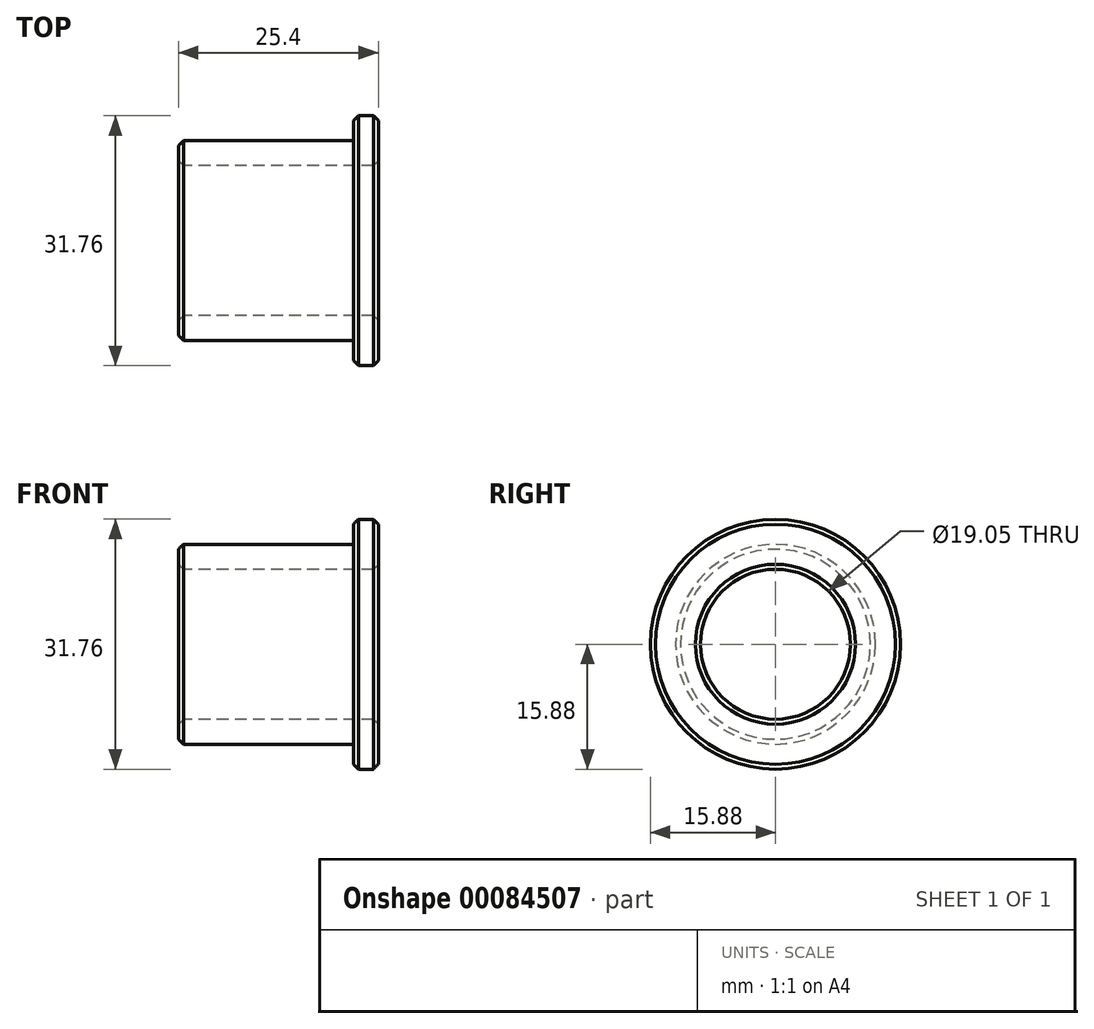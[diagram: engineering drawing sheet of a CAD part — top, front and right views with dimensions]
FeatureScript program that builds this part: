
annotation { "Feature Type Name" : "Feature", "Feature Type Description" : "" }
export const myFeature = defineFeature(function(context is Context, id is Id, definition is map)
    precondition{}
    {
        {
            var Q0;
            Q0=qCreatedBy(makeId("Front.planeOp"),FACE);
            var sketch = newSketch(context, id + "F0", { "sketchPlane" : qUnion([Q0])});
            skLineSegment(sketch, "E0", {"start": v(0, 9.52) * mm, "end": v(0, 12.7) * mm});
            skLineSegment(sketch, "E1", {"start": v(0, 12.7) * mm, "end": v(22.23, 12.7) * mm});
            skLineSegment(sketch, "E2", {"start": v(22.23, 12.7) * mm, "end": v(22.23, 15.88) * mm});
            skLineSegment(sketch, "E3", {"start": v(22.23, 15.88) * mm, "end": v(25.4, 15.88) * mm});
            skLineSegment(sketch, "E4", {"start": v(25.4, 15.88) * mm, "end": v(25.4, 9.53) * mm});
            skLineSegment(sketch, "E5", {"start": v(25.4, 9.53) * mm, "end": v(0, 9.52) * mm});
            skLineSegment(sketch, "E6", {"start": v(0, 0) * mm, "end": v(20.73, 0) * mm, "construction": true});
            skSolve(sketch);
        }
        {
            var Q0;
            Q0 = qSketchRegion(id + "F0", true);
            var Q1;
            Q1=sQuery(id+"F0.wireOp",EDGE,"E6");
            revolve(context, id + "F1", {"entities" : qUnion([Q0]), "axis" : qUnion([Q1]), "revolveType" : RevolveType.FULL});
        }
        {
            var Q0;
            Q0=makeQuery(id+"F1.opRevolve","SWEPT_EDGE",EDGE,{"disambiguationData":[OSD([sQuery(id+"F0.wireOp",EDGE,"E3"),sQuery(id+"F0.wireOp",EDGE,"E4")])]});
            var Q1;
            Q1=makeQuery(id+"F1.opRevolve","SWEPT_EDGE",EDGE,{"disambiguationData":[OSD([sQuery(id+"F0.wireOp",EDGE,"E0"),sQuery(id+"F0.wireOp",EDGE,"E1")])]});
            var Q2;
            Q2=makeQuery(id+"F1.opRevolve","SWEPT_EDGE",EDGE,{"disambiguationData":[OSD([sQuery(id+"F0.wireOp",EDGE,"E2"),sQuery(id+"F0.wireOp",EDGE,"E3")])]});
            var Q3;
            Q3=makeQuery(id+"F1.opRevolve","SWEPT_EDGE",EDGE,{"disambiguationData":[OSD([sQuery(id+"F0.wireOp",EDGE,"E4"),sQuery(id+"F0.wireOp",EDGE,"E5")])]});
            var Q4;
            Q4=makeQuery(id+"F1.opRevolve","SWEPT_EDGE",EDGE,{"disambiguationData":[OSD([sQuery(id+"F0.wireOp",EDGE,"E0"),sQuery(id+"F0.wireOp",EDGE,"E5")])]});
            chamfer(context, id + "F2", {"entities" : qUnion([Q0, Q1, Q2, Q3, Q4]), "width" : 0.64 * mm, "tangentPropagation" : true});
        }
    });
